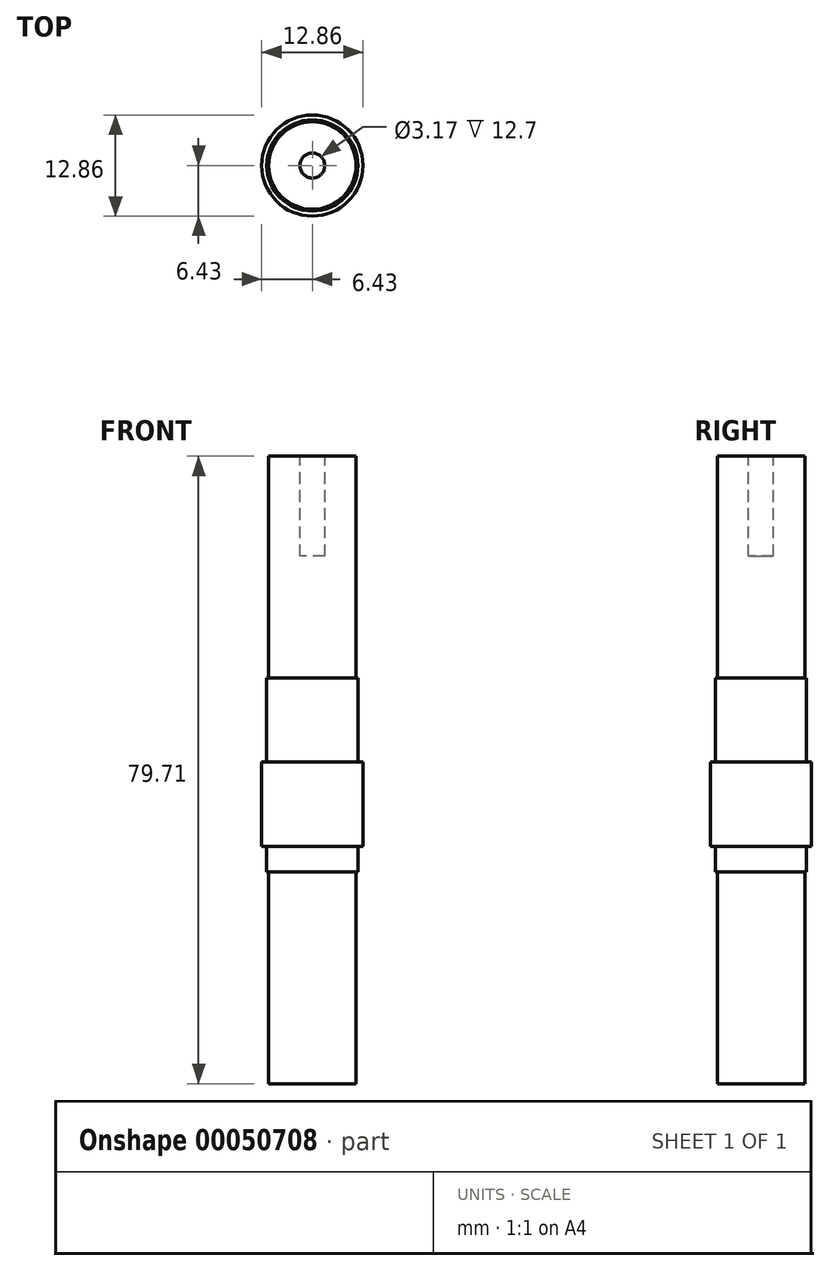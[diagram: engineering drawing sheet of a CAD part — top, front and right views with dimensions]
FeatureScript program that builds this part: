
annotation { "Feature Type Name" : "Feature", "Feature Type Description" : "" }
export const myFeature = defineFeature(function(context is Context, id is Id, definition is map)
    precondition{}
    {
        {
            var Q0;
            Q0=qCreatedBy(makeId("Top.planeOp"),FACE);
            var sketch = newSketch(context, id + "F0", { "sketchPlane" : qUnion([Q0])});
            skCircle(sketch, "E0", {"center": v(0, 0) * mm, "radius": 5.56 * mm});
            skSolve(sketch);
        }
        {
            var Q0;
            Q0=makeQuery(id+"F0.imprint","IMPRINT",FACE,{"disambiguationData":[TD([[makeQuery(id+"F0.imprint","IMPRINT",EDGE,{"derivedFrom":sQuery(id+"F0.wireOp",EDGE,"E0")}),1.0]])]});
            extrude(context, id + "F1", {"entities" : qUnion([Q0]), "depth" : 26.92 * mm});
        }
        {
            var Q0;
            Q0=makeQuery(id+"F1.opExtrude","CAP_FACE",FACE,{"disambiguationData":[OSD([sQuery(id+"F0.wireOp",EDGE,"E0")])],"isStart":false});
            var sketch = newSketch(context, id + "F2", { "sketchPlane" : qUnion([Q0])});
            skCircle(sketch, "E1", {"center": v(0, 0) * mm, "radius": 5.8 * mm});
            skSolve(sketch);
        }
        {
            var Q0;
            Q0=makeQuery(id+"F2.imprint","IMPRINT",FACE,{"disambiguationData":[TD([[makeQuery(id+"F2.imprint","IMPRINT",EDGE,{"derivedFrom":sQuery(id+"F2.wireOp",EDGE,"E1")}),1.0]])]});
            extrude(context, id + "F3", {"entities" : qUnion([Q0]), "depth" : 3.23 * mm});
        }
        {
            var Q0;
            Q0=makeQuery(id+"F1.opExtrude","CAP_FACE",FACE,{"disambiguationData":[OSD([sQuery(id+"F0.wireOp",EDGE,"E0")])],"isStart":false});
            extrude(context, id + "F4", {"entities" : qUnion([Q0]), "depth" : 3.23 * mm});
        }
        {
            var Q0;
            Q0=makeQuery(id+"F4.opExtrude","SWEPT_BODY",BODY,{"disambiguationData":[OSD([sQuery(id+"F0.wireOp",EDGE,"E0")])]});
            var Q1;
            Q1=makeQuery(id+"F3.opExtrude","SWEPT_BODY",BODY,{"disambiguationData":[OSD([sQuery(id+"F0.wireOp",EDGE,"E0"),sQuery(id+"F2.wireOp",EDGE,"E1")])]});
            booleanBodies(context, id + "F5", {"operationType" : BooleanOperationType.UNION, "tools" : qUnion([Q0, Q1])});
        }
        {
            var Q0;
            {var subQ0=sQuery(id+"F0.wireOp",EDGE,"E0");Q0=makeQuery(id+"F5.opBoolean","MERGE",FACE,{"derivedFrom":[makeQuery(id+"F3.opExtrude","CAP_FACE",FACE,{"disambiguationData":[OSD([subQ0,sQuery(id+"F2.wireOp",EDGE,"E1")])],"isStart":false}),makeQuery(id+"F4.opExtrude","CAP_FACE",FACE,{"disambiguationData":[OSD([subQ0])],"isStart":false})]});}
            var sketch = newSketch(context, id + "F6", { "sketchPlane" : qUnion([Q0])});
            skCircle(sketch, "E2", {"center": v(0, 0) * mm, "radius": 6.43 * mm});
            skSolve(sketch);
        }
        {
            var Q0;
            Q0=makeQuery(id+"F6.imprint","IMPRINT",FACE,{"disambiguationData":[TD([[makeQuery(id+"F6.imprint","IMPRINT",EDGE,{"derivedFrom":sQuery(id+"F6.wireOp",EDGE,"E2")}),1.0]])]});
            extrude(context, id + "F7", {"entities" : qUnion([Q0]), "depth" : 10.7 * mm});
        }
        {
            var Q0;
            {var subQ0=sQuery(id+"F0.wireOp",EDGE,"E0");Q0=makeQuery(id+"F5.opBoolean","MERGE",FACE,{"derivedFrom":[makeQuery(id+"F3.opExtrude","CAP_FACE",FACE,{"disambiguationData":[OSD([subQ0,sQuery(id+"F2.wireOp",EDGE,"E1")])],"isStart":false}),makeQuery(id+"F4.opExtrude","CAP_FACE",FACE,{"disambiguationData":[OSD([subQ0])],"isStart":false})]});}
            extrude(context, id + "F8", {"entities" : qUnion([Q0]), "depth" : 10.7 * mm});
        }
        {
            var Q0;
            Q0=makeQuery(id+"F8.opExtrude","SWEPT_BODY",BODY,{"disambiguationData":[OSD([sQuery(id+"F0.wireOp",EDGE,"E0"),sQuery(id+"F2.wireOp",EDGE,"E1")])]});
            var Q1;
            Q1=makeQuery(id+"F7.opExtrude","SWEPT_BODY",BODY,{"disambiguationData":[OSD([sQuery(id+"F2.wireOp",EDGE,"E1"),sQuery(id+"F6.wireOp",EDGE,"E2")])]});
            booleanBodies(context, id + "F9", {"operationType" : BooleanOperationType.UNION, "tools" : qUnion([Q0, Q1])});
        }
        {
            var Q0;
            {var subQ0=sQuery(id+"F2.wireOp",EDGE,"E1");Q0=makeQuery(id+"F9.opBoolean","MERGE",FACE,{"derivedFrom":[makeQuery(id+"F7.opExtrude","CAP_FACE",FACE,{"disambiguationData":[OSD([subQ0,sQuery(id+"F6.wireOp",EDGE,"E2")])],"isStart":false}),makeQuery(id+"F8.opExtrude","CAP_FACE",FACE,{"disambiguationData":[OSD([sQuery(id+"F0.wireOp",EDGE,"E0"),subQ0])],"isStart":false})]});}
            var sketch = newSketch(context, id + "F10", { "sketchPlane" : qUnion([Q0])});
            skCircle(sketch, "E3", {"center": v(0, 0) * mm, "radius": 5.8 * mm});
            skSolve(sketch);
        }
        {
            var Q0;
            Q0 = qSketchRegion(id + "F10", true);
            extrude(context, id + "F11", {"entities" : qUnion([Q0]), "operationType" : NewBodyOperationType.ADD, "depth" : 10.7 * mm});
        }
        {
            var Q0;
            Q0=makeQuery(id+"F11.opExtrude","CAP_FACE",FACE,{"disambiguationData":[OSD([sQuery(id+"F10.wireOp",EDGE,"E3")])],"isStart":false});
            var sketch = newSketch(context, id + "F12", { "sketchPlane" : qUnion([Q0])});
            skCircle(sketch, "E4", {"center": v(0, 0) * mm, "radius": 5.56 * mm});
            skSolve(sketch);
        }
        {
            var Q0;
            Q0=makeQuery(id+"F12.imprint","IMPRINT",FACE,{"disambiguationData":[TD([[makeQuery(id+"F12.imprint","IMPRINT",EDGE,{"derivedFrom":sQuery(id+"F12.wireOp",EDGE,"E4")}),1.0]])]});
            extrude(context, id + "F13", {"entities" : qUnion([Q0]), "operationType" : NewBodyOperationType.ADD, "depth" : 28.17 * mm});
        }
        {
            var Q0;
            Q0=makeQuery(id+"F13.opExtrude","CAP_FACE",FACE,{"disambiguationData":[OSD([sQuery(id+"F12.wireOp",EDGE,"E4")])],"isStart":false});
            var sketch = newSketch(context, id + "F14", { "sketchPlane" : qUnion([Q0])});
            skCircle(sketch, "E5", {"center": v(0, 0) * mm, "radius": 1.59 * mm});
            skSolve(sketch);
        }
        {
            var Q0;
            Q0=makeQuery(id+"F14.imprint","IMPRINT",FACE,{"disambiguationData":[TD([[makeQuery(id+"F14.imprint","IMPRINT",EDGE,{"derivedFrom":sQuery(id+"F14.wireOp",EDGE,"E5")}),-1.0]])]});
            var sketch = newSketch(context, id + "F15", { "sketchPlane" : qUnion([Q0])});
            skSolve(sketch);
        }
        {
            var Q0;
            Q0 = qSketchRegion(id + "F15", true);
            var Q1;
            Q1=makeQuery(id+"F14.imprint","IMPRINT",FACE,{"disambiguationData":[TD([[makeQuery(id+"F14.imprint","IMPRINT",EDGE,{"derivedFrom":sQuery(id+"F14.wireOp",EDGE,"E5")}),1.0]])]});
            extrude(context, id + "F16", {"entities" : qUnion([Q0, Q1]), "operationType" : NewBodyOperationType.REMOVE, "oppositeDirection" : true, "depth" : 12.7 * mm});
        }
    });
